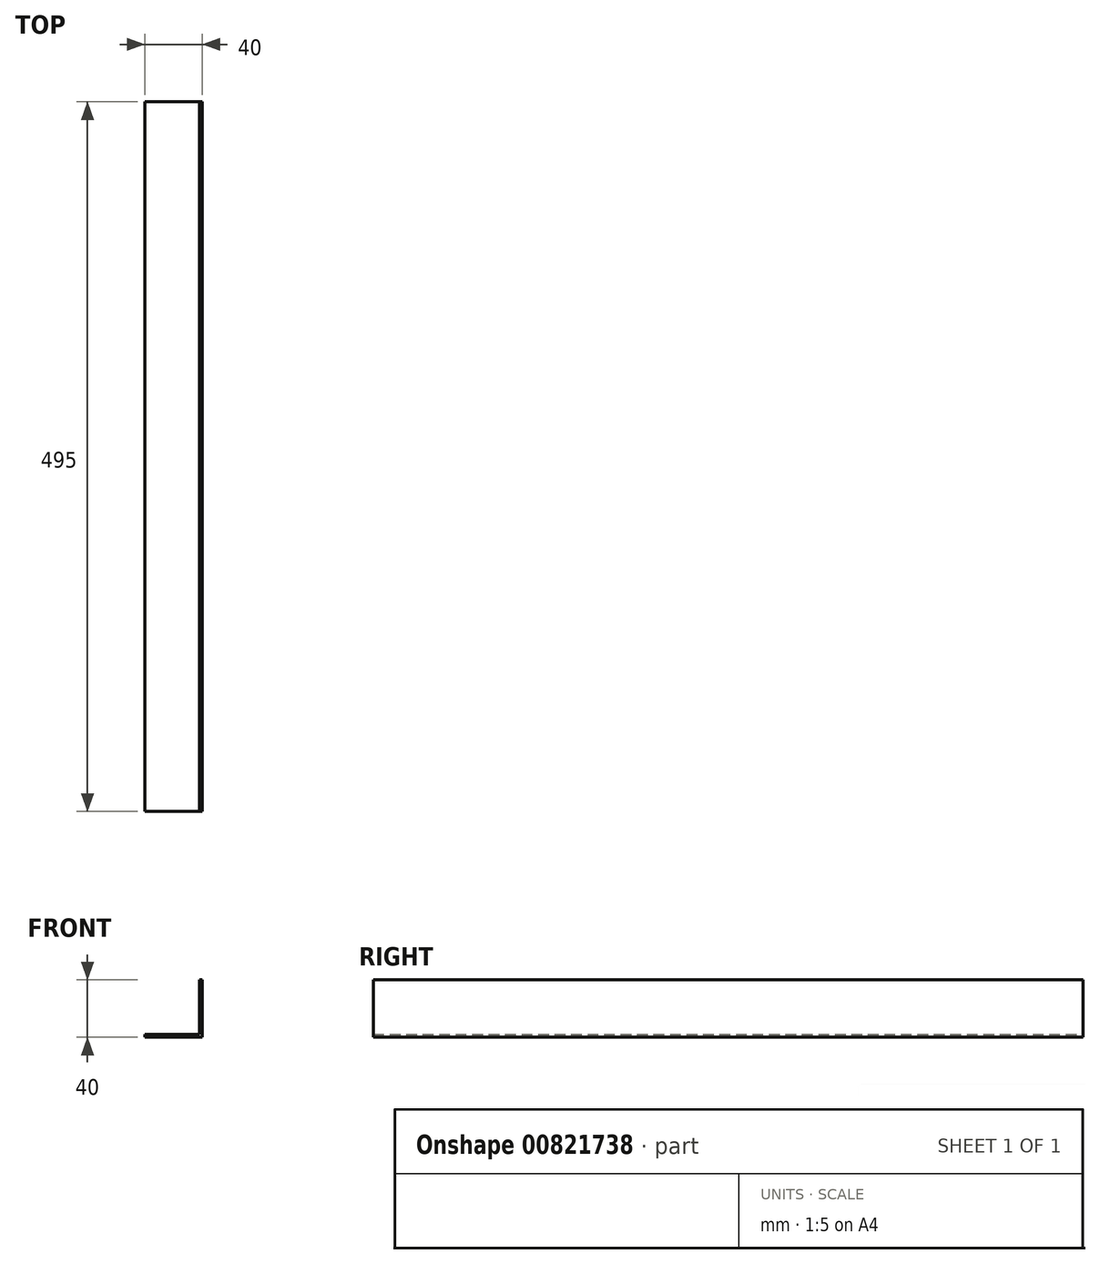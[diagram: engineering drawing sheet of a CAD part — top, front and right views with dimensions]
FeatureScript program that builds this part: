
annotation { "Feature Type Name" : "Feature", "Feature Type Description" : "" }
export const myFeature = defineFeature(function(context is Context, id is Id, definition is map)
    precondition{}
    {
        {
            var Q0;
            Q0=qCreatedBy(makeId("Front.planeOp"),FACE);
            var sketch = newSketch(context, id + "F0", { "sketchPlane" : qUnion([Q0])});
            skLineSegment(sketch, "E0", {"start": v(0, 0) * mm, "end": v(-40, 0) * mm});
            skLineSegment(sketch, "E1", {"start": v(-40, 0) * mm, "end": v(-40, 2) * mm});
            skLineSegment(sketch, "E2", {"start": v(-40, 2) * mm, "end": v(-2, 2) * mm});
            skLineSegment(sketch, "E3", {"start": v(-2, 2) * mm, "end": v(-2, 40) * mm});
            skLineSegment(sketch, "E4", {"start": v(-2, 40) * mm, "end": v(0, 40) * mm});
            skLineSegment(sketch, "E5", {"start": v(0, 40) * mm, "end": v(0, 0) * mm});
            skSolve(sketch);
        }
        {
            var Q0;
            Q0=qSketchRegion(id+"F0",true);
            extrude(context, id + "F1", {"entities" : qUnion([Q0]), "depth" : 495 * mm, "offsetDistance" : 25 * mm});
        }
    });
